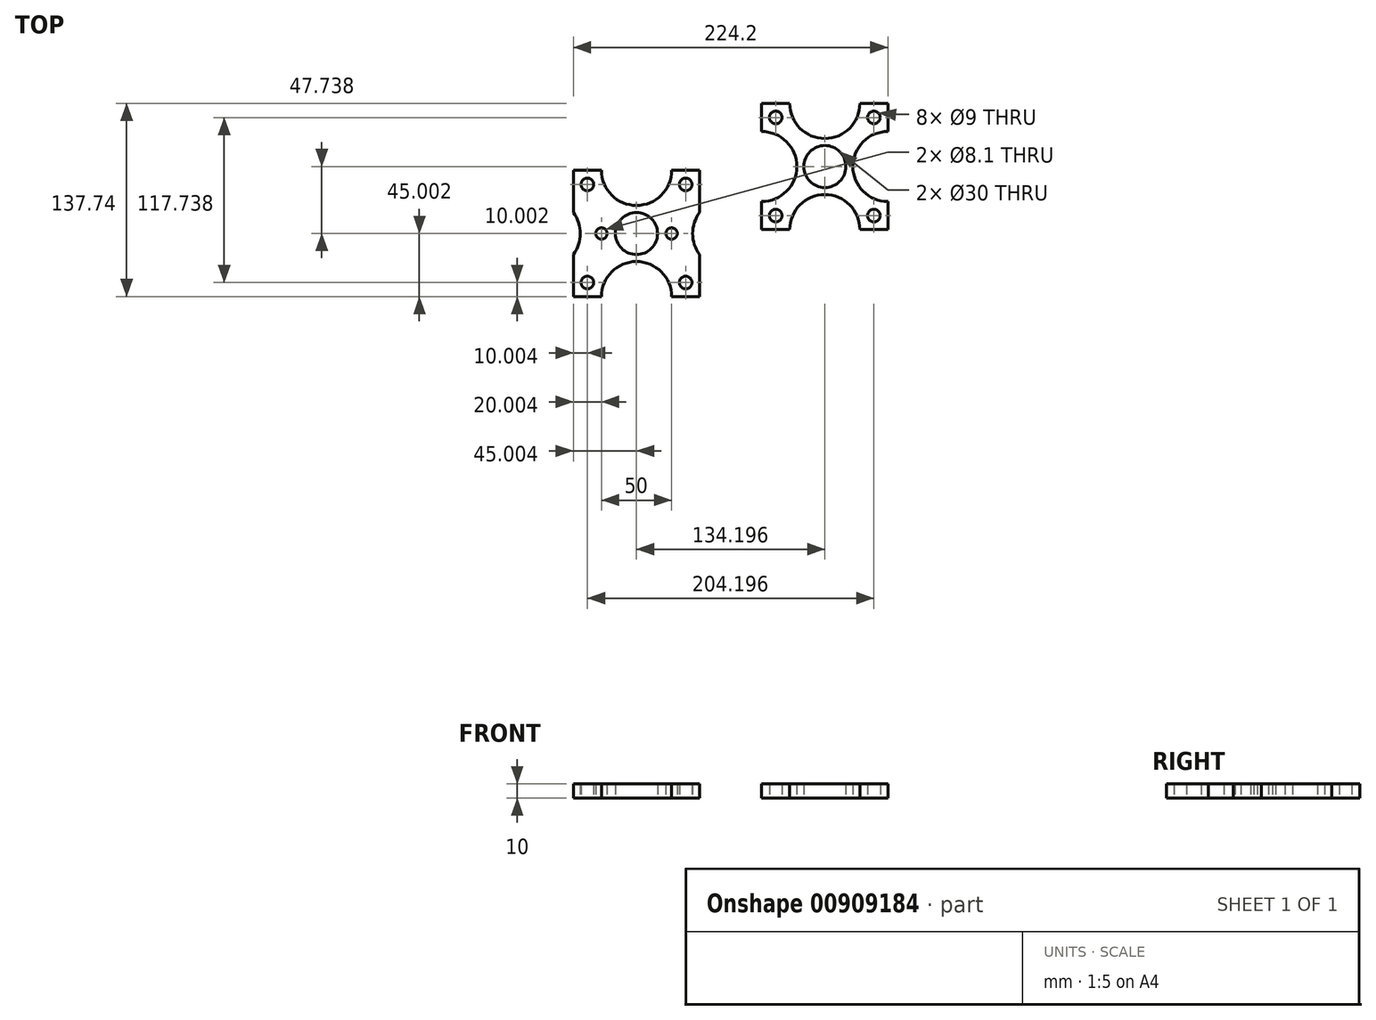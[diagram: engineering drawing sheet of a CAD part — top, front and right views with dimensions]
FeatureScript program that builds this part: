
annotation { "Feature Type Name" : "Feature", "Feature Type Description" : "" }
export const myFeature = defineFeature(function(context is Context, id is Id, definition is map)
    precondition{}
    {
        {
            var Q0;
            Q0=qCreatedBy(makeId("Top.planeOp"),FACE);
            var sketch = newSketch(context, id + "F0", { "sketchPlane" : qUnion([Q0])});
            skLineSegment(sketch, "E0.bottom", {"start": v(0, 0) * mm, "end": v(90, 0) * mm});
            skLineSegment(sketch, "E0.top", {"start": v(0, 90) * mm, "end": v(90, 90) * mm});
            skLineSegment(sketch, "E0.left", {"start": v(0, 0) * mm, "end": v(0, 90) * mm});
            skLineSegment(sketch, "E0.right", {"start": v(90, 0) * mm, "end": v(90, 90) * mm});
            skCircle(sketch, "E1", {"center": v(10, 80) * mm, "radius": 4.5 * mm});
            skCircle(sketch, "E2.0.1.0", {"center": v(10, 10) * mm, "radius": 4.5 * mm});
            skCircle(sketch, "E2.1.0.0", {"center": v(80, 80) * mm, "radius": 4.5 * mm});
            skCircle(sketch, "E2.1.1.0", {"center": v(80, 10) * mm, "radius": 4.5 * mm});
            skLineSegment(sketch, "E2.direction1", {"start": v(10, 80) * mm, "end": v(80, 80) * mm, "construction": true});
            skLineSegment(sketch, "E2.direction2", {"start": v(10, 80) * mm, "end": v(10, 10) * mm, "construction": true});
            skCircle(sketch, "E3", {"center": v(45, 90) * mm, "radius": 25 * mm});
            skCircle(sketch, "E4.1.0", {"center": v(90, 45) * mm, "radius": 25 * mm});
            skCircle(sketch, "E4.2.0", {"center": v(45, 0) * mm, "radius": 25 * mm});
            skCircle(sketch, "E4.3.0", {"center": v(0, 45) * mm, "radius": 25 * mm});
            skPoint(sketch, "E4.center", {"position": v(45, 45) * mm});
            skLineSegment(sketch, "E4.anchor1", {"start": v(45, 45) * mm, "end": v(45, 90) * mm, "construction": true});
            skLineSegment(sketch, "E4.anchor2", {"start": v(45, 45) * mm, "end": v(0, 45) * mm, "construction": true});
            skLineSegment(sketch, "E5", {"start": v(90, 45) * mm, "end": v(0, 45) * mm});
            skLineSegment(sketch, "E6", {"start": v(45, 0) * mm, "end": v(45, 90) * mm});
            skCircle(sketch, "E7", {"center": v(45, 45) * mm, "radius": 15 * mm});
            skSolve(sketch);
        }
        {
            var Q0;
            Q0=makeQuery(id+"F0.imprint","IMPRINT",FACE,{"disambiguationData":[TD([[makeQuery(id+"F0.imprint","IMPRINT",EDGE,{"derivedFrom":sQuery(id+"F0.wireOp",EDGE,"E1")}),-1.0]])]});
            var Q1;
            Q1=makeQuery(id+"F0.imprint","IMPRINT",FACE,{"disambiguationData":[TD([[makeQuery(id+"F0.imprint","IMPRINT",EDGE,{"derivedFrom":sQuery(id+"F0.wireOp",EDGE,"E2.1.0.0")}),-1.0]])]});
            var Q2;
            Q2=makeQuery(id+"F0.imprint","IMPRINT",FACE,{"disambiguationData":[TD([[makeQuery(id+"F0.imprint","IMPRINT",EDGE,{"derivedFrom":sQuery(id+"F0.wireOp",EDGE,"E2.1.1.0")}),-1.0]])]});
            var Q3;
            Q3=makeQuery(id+"F0.imprint","IMPRINT",FACE,{"disambiguationData":[TD([[makeQuery(id+"F0.imprint","IMPRINT",EDGE,{"derivedFrom":sQuery(id+"F0.wireOp",EDGE,"E2.0.1.0")}),-1.0]])]});
            extrude(context, id + "F1", {"entities" : qUnion([Q0, Q1, Q2, Q3]), "depth" : 10 * mm, "offsetDistance" : 25 * mm});
        }
        {
            var Q0;
            Q0=qCreatedBy(makeId("Top.planeOp"),FACE);
            var sketch = newSketch(context, id + "F2", { "sketchPlane" : qUnion([Q0])});
            skLineSegment(sketch, "E8.bottom", {"start": v(-134.2, -47.74) * mm, "end": v(-44.2, -47.74) * mm});
            skLineSegment(sketch, "E8.top", {"start": v(-134.2, 42.26) * mm, "end": v(-44.2, 42.26) * mm});
            skLineSegment(sketch, "E8.left", {"start": v(-134.2, -47.74) * mm, "end": v(-134.2, 42.26) * mm});
            skLineSegment(sketch, "E8.right", {"start": v(-44.2, -47.74) * mm, "end": v(-44.2, 42.26) * mm});
            skCircle(sketch, "E9", {"center": v(-124.2, 32.26) * mm, "radius": 4.5 * mm});
            skCircle(sketch, "E10.0.1.0", {"center": v(-124.2, -37.74) * mm, "radius": 4.5 * mm});
            skCircle(sketch, "E10.1.0.0", {"center": v(-54.2, 32.26) * mm, "radius": 4.5 * mm});
            skCircle(sketch, "E10.1.1.0", {"center": v(-54.2, -37.74) * mm, "radius": 4.5 * mm});
            skLineSegment(sketch, "E10.direction1", {"start": v(-124.2, 32.26) * mm, "end": v(-54.2, 32.26) * mm, "construction": true});
            skLineSegment(sketch, "E10.direction2", {"start": v(-124.2, 32.26) * mm, "end": v(-124.2, -37.74) * mm, "construction": true});
            skCircle(sketch, "E11", {"center": v(-89.2, 42.26) * mm, "radius": 25 * mm});
            skCircle(sketch, "E12.2.0", {"center": v(-89.2, -47.74) * mm, "radius": 25 * mm});
            skPoint(sketch, "E12.center", {"position": v(-89.2, -2.74) * mm});
            skLineSegment(sketch, "E12.anchor1", {"start": v(-89.2, -2.74) * mm, "end": v(-89.2, 42.26) * mm, "construction": true});
            skLineSegment(sketch, "E12.anchor2", {"start": v(-89.2, -2.74) * mm, "end": v(-134.2, -2.74) * mm, "construction": true});
            skLineSegment(sketch, "E13", {"start": v(-44.2, -2.74) * mm, "end": v(-134.2, -2.74) * mm});
            skLineSegment(sketch, "E14", {"start": v(-89.2, -47.74) * mm, "end": v(-89.2, 42.26) * mm});
            skCircle(sketch, "E15", {"center": v(-89.2, -2.74) * mm, "radius": 15 * mm});
            skLineSegment(sketch, "E16", {"start": v(-134.2, -2.74) * mm, "end": v(-154.2, -2.74) * mm});
            skLineSegment(sketch, "E17", {"start": v(-44.2, -2.74) * mm, "end": v(-24.2, -2.74) * mm});
            skCircle(sketch, "E18", {"center": v(-154.2, -2.74) * mm, "radius": 25 * mm});
            skCircle(sketch, "E19", {"center": v(-24.2, -2.74) * mm, "radius": 25 * mm});
            skCircle(sketch, "E20", {"center": v(-114.2, -2.74) * mm, "radius": 4.05 * mm});
            skCircle(sketch, "E21", {"center": v(-64.2, -2.74) * mm, "radius": 4.05 * mm});
            skSolve(sketch);
        }
        {
            var Q0;
            Q0=makeQuery(id+"F2.imprint","IMPRINT",FACE,{"disambiguationData":[TD([[makeQuery(id+"F2.imprint","IMPRINT",EDGE,{"derivedFrom":sQuery(id+"F2.wireOp",EDGE,"E9")}),-1.0]])]});
            var Q1;
            Q1=makeQuery(id+"F2.imprint","IMPRINT",FACE,{"disambiguationData":[TD([[makeQuery(id+"F2.imprint","IMPRINT",EDGE,{"derivedFrom":sQuery(id+"F2.wireOp",EDGE,"E10.1.0.0")}),-1.0]])]});
            var Q2;
            Q2=makeQuery(id+"F2.imprint","IMPRINT",FACE,{"disambiguationData":[TD([[makeQuery(id+"F2.imprint","IMPRINT",EDGE,{"derivedFrom":sQuery(id+"F2.wireOp",EDGE,"E10.1.1.0")}),-1.0]])]});
            var Q3;
            Q3=makeQuery(id+"F2.imprint","IMPRINT",FACE,{"disambiguationData":[TD([[makeQuery(id+"F2.imprint","IMPRINT",EDGE,{"derivedFrom":sQuery(id+"F2.wireOp",EDGE,"E10.0.1.0")}),-1.0]])]});
            extrude(context, id + "F3", {"entities" : qUnion([Q0, Q1, Q2, Q3]), "depth" : 10 * mm, "offsetDistance" : 25 * mm});
        }
    });
